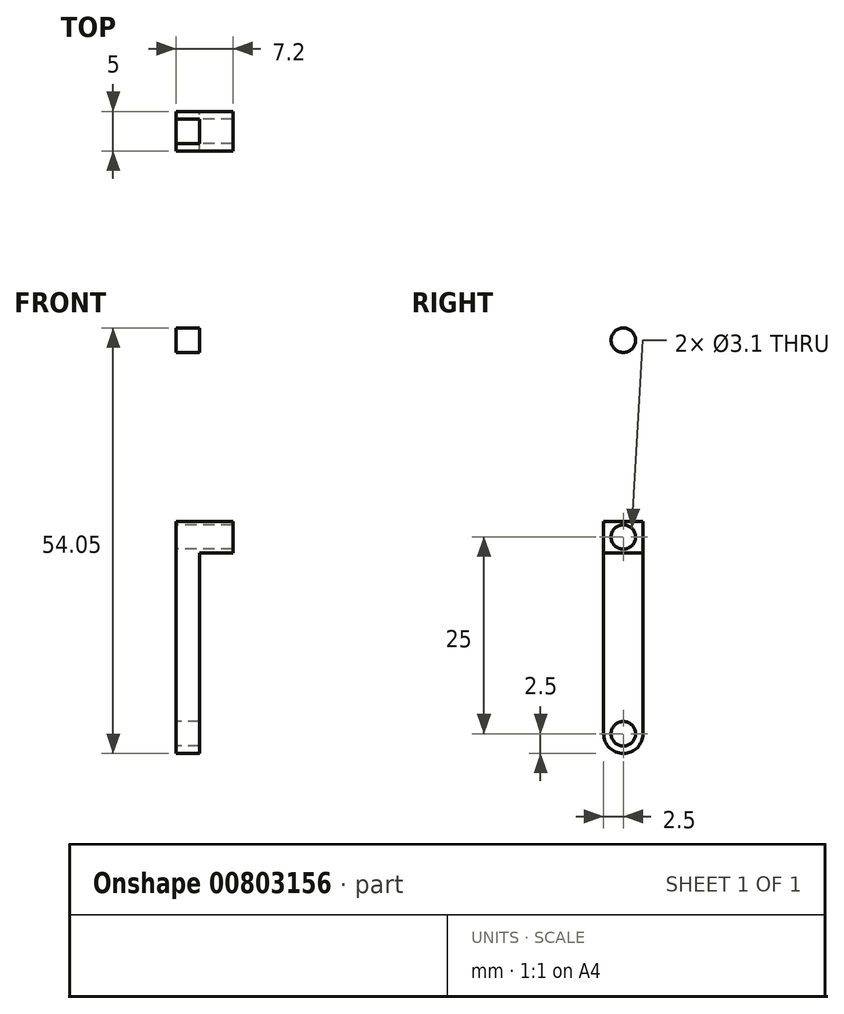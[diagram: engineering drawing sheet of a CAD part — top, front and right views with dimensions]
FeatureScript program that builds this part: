
annotation { "Feature Type Name" : "Feature", "Feature Type Description" : "" }
export const myFeature = defineFeature(function(context is Context, id is Id, definition is map)
    precondition{}
    {
        {
            var Q0;
            Q0=qCreatedBy(makeId("Right.planeOp"),FACE);
            var sketch = newSketch(context, id + "F0", { "sketchPlane" : qUnion([Q0])});
            skCircle(sketch, "E0", {"center": v(0, 0) * mm, "radius": 1.55 * mm});
            skArc(sketch, "E1", {"start": v(-2.5, 0) * mm, "mid": v(0, -2.5) * mm, "end": v(2.5, 0) * mm});
            skLineSegment(sketch, "E2", {"start": v(-2.5, 0) * mm, "end": v(-2.5, 50) * mm});
            skLineSegment(sketch, "E3", {"start": v(2.5, 50) * mm, "end": v(2.5, 0) * mm});
            skLineSegment(sketch, "E4", {"start": v(-2.5, 25) * mm, "end": v(0, 25) * mm, "construction": true});
            skCircle(sketch, "E5.MirrorC", {"center": v(0, 50) * mm, "radius": 1.55 * mm});
            skArc(sketch, "E6.MirrorCS", {"start": v(-2.5, 50) * mm, "mid": v(0, 52.5) * mm, "end": v(2.5, 50) * mm});
            skLineSegment(sketch, "E7.bottom", {"start": v(-2.5, 27) * mm, "end": v(2.5, 27) * mm});
            skLineSegment(sketch, "E7.top", {"start": v(-2.5, 23) * mm, "end": v(2.5, 23) * mm});
            skLineSegment(sketch, "E7.left", {"start": v(-2.5, 27) * mm, "end": v(-2.5, 23) * mm});
            skLineSegment(sketch, "E7.right", {"start": v(2.5, 27) * mm, "end": v(2.5, 23) * mm});
            skPoint(sketch, "E7.middle", {"position": v(0, 25) * mm});
            skCircle(sketch, "E8", {"center": v(0, 25) * mm, "radius": 1.55 * mm});
            skSolve(sketch);
        }
        {
            var Q0;
            Q0=makeQuery(id+"F0.imprint","IMPRINT",FACE,{"disambiguationData":[TD([[makeQuery(id+"F0.imprint","IMPRINT",EDGE,{"derivedFrom":sQuery(id+"F0.wireOp",EDGE,"E5.MirrorC")}),1.0]])]});
            var Q1;
            {var subQ1=sQuery(id+"F0.wireOp",EDGE,"E7.bottom");Q1=makeQuery(id+"F0.imprint","IMPRINT",FACE,{"disambiguationData":[TD([[makeQuery(id+"F0.imprint","IMPRINT",EDGE,{"derivedFrom":subQ1}),-1.0]])]});}
            var Q2;
            Q2=makeQuery(id+"F0.imprint","IMPRINT",FACE,{"disambiguationData":[TD([[makeQuery(id+"F0.imprint","IMPRINT",EDGE,{"derivedFrom":sQuery(id+"F0.wireOp",EDGE,"E0")}),-1.0]])]});
            extrude(context, id + "F1", {"entities" : qUnion([Q0, Q1, Q2]), "depth" : 3 * mm, "offsetDistance" : 25 * mm});
        }
        {
            var Q0;
            {var subQ1=sQuery(id+"F0.wireOp",EDGE,"E7.bottom");Q0=makeQuery(id+"F0.imprint","IMPRINT",FACE,{"disambiguationData":[TD([[makeQuery(id+"F0.imprint","IMPRINT",EDGE,{"derivedFrom":subQ1}),-1.0]])]});}
            extrude(context, id + "F2", {"entities" : qUnion([Q0]), "operationType" : NewBodyOperationType.ADD, "depth" : 7.2 * mm, "offsetDistance" : 25 * mm});
        }
    });
